# Revit family: Zline 90
name_source: partatom
category: Modèles génériques
units: mm (PartAtom-declared; Revit-internal decimal feet)

## family parameters
Basée sur le plan de construction = Non
Cote de connecteur circulaire = Utiliser le diamètre
Couper avec des vides une fois chargée = Non
Partagée = Non
Peut héberger une armature = Oui
Point de calcul de pièce = Non
Toujours verticalement = Oui
Type d'élément = Normal

## types (1)
- Zline 90
    Distance lame finale = 63 mm  [stored 0.206693 ft]
    Distance ruban = 1050 mm  [stored 3.44488 ft]
    Distance étrier = 997 mm
    Elévation par défaut = 0 mm  [stored 0 ft]
    Hauteur Maxi = 4500 mm
    Hauteur mini = 500 mm  [stored 1.64042 ft]
    Hauteur ruban = 2413 mm
    Hauteur souhaitée = 2500 mm  [stored 8.2021 ft]
    Hauteur_coulisse = 2439 mm  [stored 8.00197 ft]
    Hauteur_rail = 57 mm  [stored 0.187008 ft]
    Hauteur_totale = 2500 mm  [stored 8.2021 ft]
    Inclinaison lames = 0.00°
    Lame 0 = Non
    Lame 45 = Non
    Lame 90 = Non
    Longueur Maxi = 5000 mm  [stored 16.4042 ft]
    Longueur lame = 2450 mm  [stored 8.03806 ft]
    Longueur mini = 580 mm  [stored 1.90289 ft]
    Longueur souhaitée = 2500 mm  [stored 8.2021 ft]
    Longueur_rail = 2490 mm  [stored 8.16929 ft]
    Longueur_totale = 2500 mm  [stored 8.2021 ft]
    Materiau = Aluminium
    Nombre d'étrier = 3
    Nombre lame = 30
    Nombre ruban = 3
    Plié = Non
    distance lame = 78 mm  [stored 0.255906 ft]
    inclinaison lame finale = 0.00°

note: [stored X ft] marks values corroborated as IEEE doubles in the binary element streams (Revit-internal decimal feet)

## geometry (parser evidence)
native form markers: Blend x12, Sweep x6
no freeform markers — native parametric forms only
